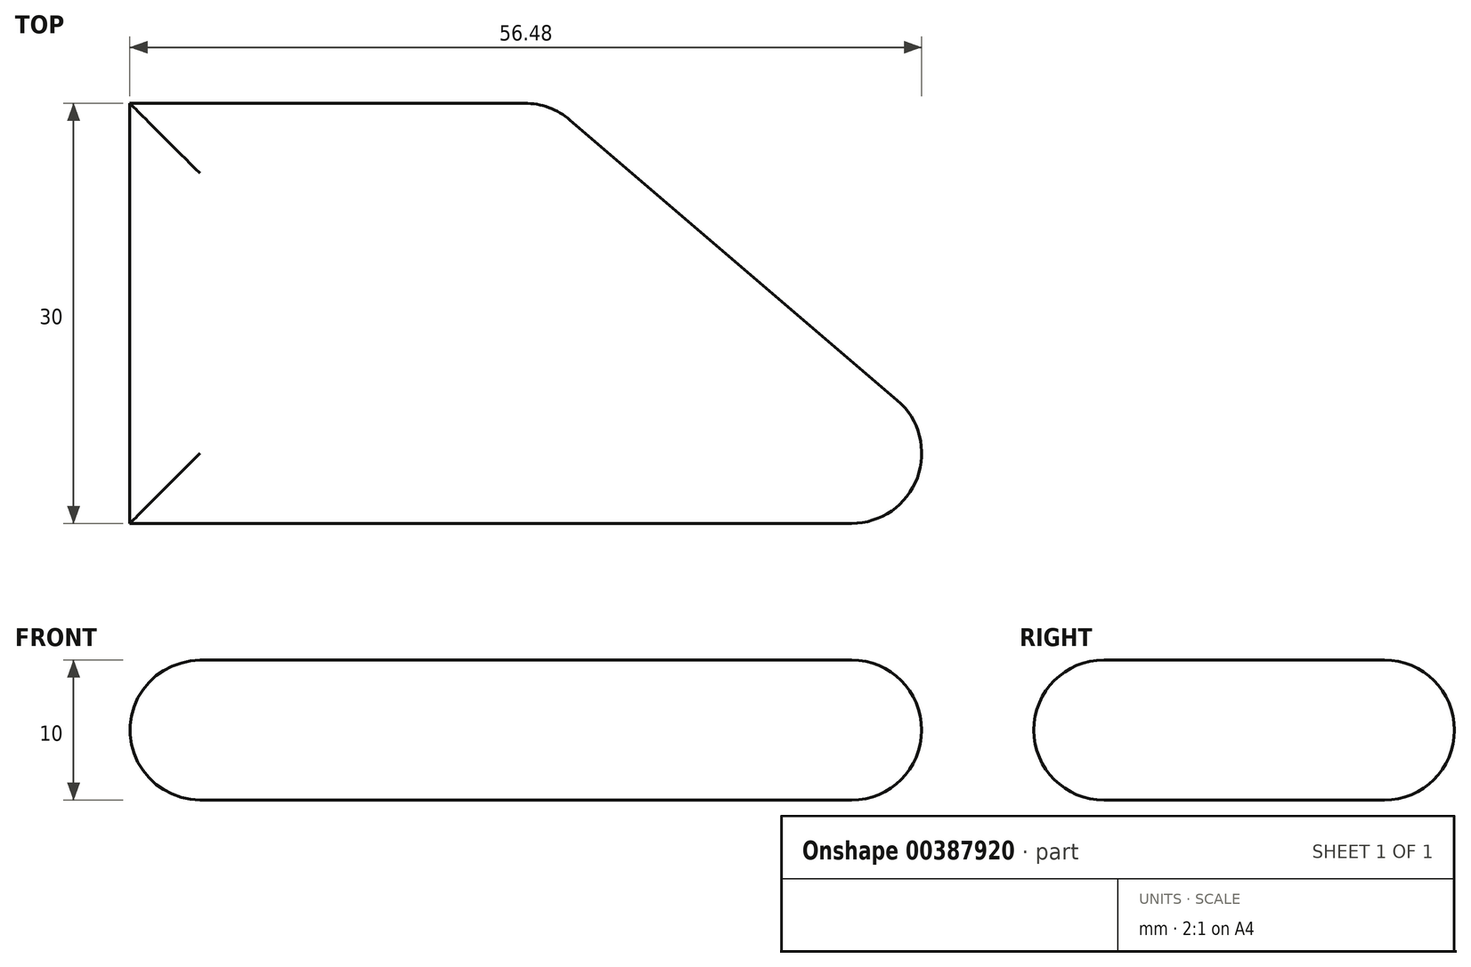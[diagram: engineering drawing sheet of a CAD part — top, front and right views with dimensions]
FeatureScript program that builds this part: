
annotation { "Feature Type Name" : "Feature", "Feature Type Description" : "" }
export const myFeature = defineFeature(function(context is Context, id is Id, definition is map)
    precondition{}
    {
        {
            var Q0;
            Q0=qCreatedBy(makeId("Top.planeOp"),FACE);
            var sketch = newSketch(context, id + "F0", { "sketchPlane" : qUnion([Q0])});
            skLineSegment(sketch, "E0.bottom", {"start": v(-65, 58.65) * mm, "end": v(-35, 58.65) * mm});
            skLineSegment(sketch, "E0.top", {"start": v(-65, 28.65) * mm, "end": v(-35, 28.65) * mm});
            skLineSegment(sketch, "E0.left", {"start": v(-65, 58.65) * mm, "end": v(-65, 28.65) * mm});
            skLineSegment(sketch, "E0.right", {"start": v(-35, 58.65) * mm, "end": v(-35, 28.65) * mm});
            skLineSegment(sketch, "E1", {"start": v(-35, 28.65) * mm, "end": v(0, 28.65) * mm});
            skLineSegment(sketch, "E2", {"start": v(0, 28.65) * mm, "end": v(-35, 58.65) * mm});
            skSolve(sketch);
        }
        {
            var Q0;
            Q0=makeQuery(id+"F0.imprint","IMPRINT",FACE,{"disambiguationData":[TD([[makeQuery(id+"F0.imprint","IMPRINT",EDGE,{"derivedFrom":sQuery(id+"F0.wireOp",EDGE,"E0.right")}),1.0]])]});
            var Q1;
            Q1=makeQuery(id+"F0.imprint","IMPRINT",FACE,{"disambiguationData":[TD([[makeQuery(id+"F0.imprint","IMPRINT",EDGE,{"derivedFrom":sQuery(id+"F0.wireOp",EDGE,"E0.bottom")}),-1.0]])]});
            extrude(context, id + "F1", {"entities" : qUnion([Q0, Q1]), "depth" : 10 * mm});
        }
        {
            var Q0;
            Q0=makeQuery(id+"F1.opExtrude","CAP_FACE",FACE,{"disambiguationData":[OSD([sQuery(id+"F0.wireOp",EDGE,"E0.bottom"),sQuery(id+"F0.wireOp",EDGE,"E0.top"),sQuery(id+"F0.wireOp",EDGE,"E0.left"),sQuery(id+"F0.wireOp",EDGE,"E1"),sQuery(id+"F0.wireOp",EDGE,"E2")])],"isStart":false});
            var Q1;
            Q1=makeQuery(id+"F1.opExtrude","CAP_EDGE",EDGE,{"disambiguationData":[OSD([sQuery(id+"F0.wireOp",EDGE,"E0.top"),sQuery(id+"F0.wireOp",EDGE,"E1")])],"isStart":true});
            var Q2;
            Q2=makeQuery(id+"F1.opExtrude","CAP_EDGE",EDGE,{"disambiguationData":[OSD([sQuery(id+"F0.wireOp",EDGE,"E0.left")])],"isStart":true});
            var Q3;
            Q3=makeQuery(id+"F1.opExtrude","CAP_EDGE",EDGE,{"disambiguationData":[OSD([sQuery(id+"F0.wireOp",EDGE,"E0.bottom")])],"isStart":true});
            var Q4;
            Q4=makeQuery(id+"F1.opExtrude","CAP_EDGE",EDGE,{"disambiguationData":[OSD([sQuery(id+"F0.wireOp",EDGE,"E2")])],"isStart":true});
            var Q5;
            Q5=makeQuery(id+"F1.opExtrude","CAP_EDGE",EDGE,{"disambiguationData":[OSD([sQuery(id+"F0.wireOp",EDGE,"E2")])],"isStart":false});
            var Q6;
            Q6=makeQuery(id+"F1.opExtrude","SWEPT_EDGE",EDGE,{"disambiguationData":[OSD([sQuery(id+"F0.wireOp",EDGE,"E0.bottom"),sQuery(id+"F0.wireOp",EDGE,"E0.right"),sQuery(id+"F0.wireOp",EDGE,"E2")])]});
            var Q7;
            Q7=makeQuery(id+"F1.opExtrude","SWEPT_EDGE",EDGE,{"disambiguationData":[OSD([sQuery(id+"F0.wireOp",EDGE,"E1"),sQuery(id+"F0.wireOp",EDGE,"E2")])]});
            fillet(context, id + "F2", {"entities" : qUnion([Q0, Q1, Q2, Q3, Q4, Q5, Q6, Q7]), "radius" : 5 * mm, "tangentPropagation" : true, "allowEdgeOverflow" : false});
        }
    });
